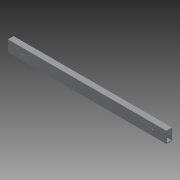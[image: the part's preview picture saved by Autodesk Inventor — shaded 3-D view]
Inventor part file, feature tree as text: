
AUTODESK INVENTOR PART (.ipt)
format: ipt  version: 2015 SP1 (Build 190203100, 203)  size: 90,112 bytes
history: native  units: in
note: dims shown in document units (in); Inventor stores cm internally (conversion verified against a paired STEP export)
features: sketch x2, extrude x1, hole x1, projected_geometry x1
ambient origin geometry x8: Origin, YZ Plane, XZ Plane, XY Plane, X Axis, Y Axis, Z Axis, Center Point
bodies: Solid1 (feature_tree)
feature tree (5):
  extrude  "Extrusion1"  Depth=1.0in
  hole  "Hole3"  [1 undecoded]
  sketch  "Sketch1"  dims[d0=2.0in d1=1.0in]
  sketch  "Sketch2"  dims[d2=1.75in d3=0.75in d4=0.125in d5=0.125in d6=28.0in d7=0.0in d8=2.5in d9=1.0in d10=2.5in d11=1.0in d30=0.25in d31=0.75in d32=0.375in d33=0.25in d34=0.5635in d35=1.0in d36=0.8108in]
  projected_geometry  "Projected Loop1"
note: 1 required parameter value undecoded (feature->parameter linkage not recoverable at this tier; creation-order binding heuristic only, values carry confidence <= 0.55)
